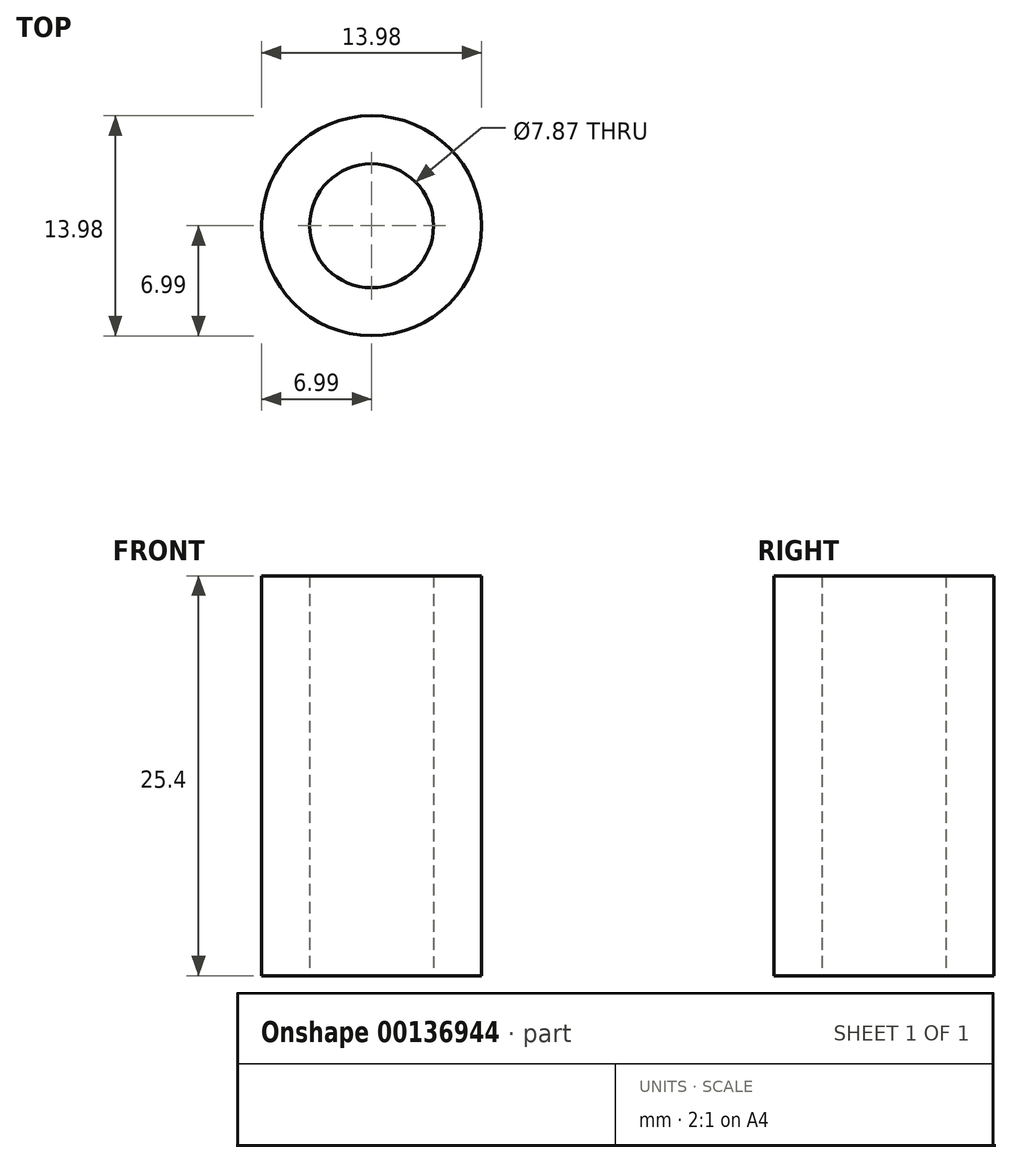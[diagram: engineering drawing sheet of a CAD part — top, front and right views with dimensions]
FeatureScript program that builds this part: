
annotation { "Feature Type Name" : "Feature", "Feature Type Description" : "" }
export const myFeature = defineFeature(function(context is Context, id is Id, definition is map)
    precondition{}
    {
        {
            var Q0;
            Q0=qCreatedBy(makeId("Top.planeOp"),FACE);
            var sketch = newSketch(context, id + "F0", { "sketchPlane" : qUnion([Q0])});
            skCircle(sketch, "E0", {"center": v(0, 0) * mm, "radius": 6.99 * mm});
            skSolve(sketch);
        }
        {
            var Q0;
            Q0 = qSketchRegion(id + "F0", true);
            extrude(context, id + "F1", {"entities" : qUnion([Q0]), "depth" : 25.4 * mm});
        }
        {
            var Q0;
            Q0=makeQuery(id+"F1.opExtrude","CAP_FACE",FACE,{"disambiguationData":[OSD([sQuery(id+"F0.wireOp",EDGE,"E0")])],"isStart":false});
            var Q1;
            Q1=makeQuery(id+"F1.opExtrude","CAP_FACE",FACE,{"disambiguationData":[OSD([sQuery(id+"F0.wireOp",EDGE,"E0")])],"isStart":true});
            var Q2;
            Q2=makeQuery(id+"F1.opExtrude","SWEPT_BODY",BODY,{"disambiguationData":[OSD([sQuery(id+"F0.wireOp",EDGE,"E0")])]});
            shell(context, id + "F2", {"entities" : qUnion([Q0, Q1]), "parts" : qUnion([Q2]), "thickness" : 3.05 * mm});
        }
    });
